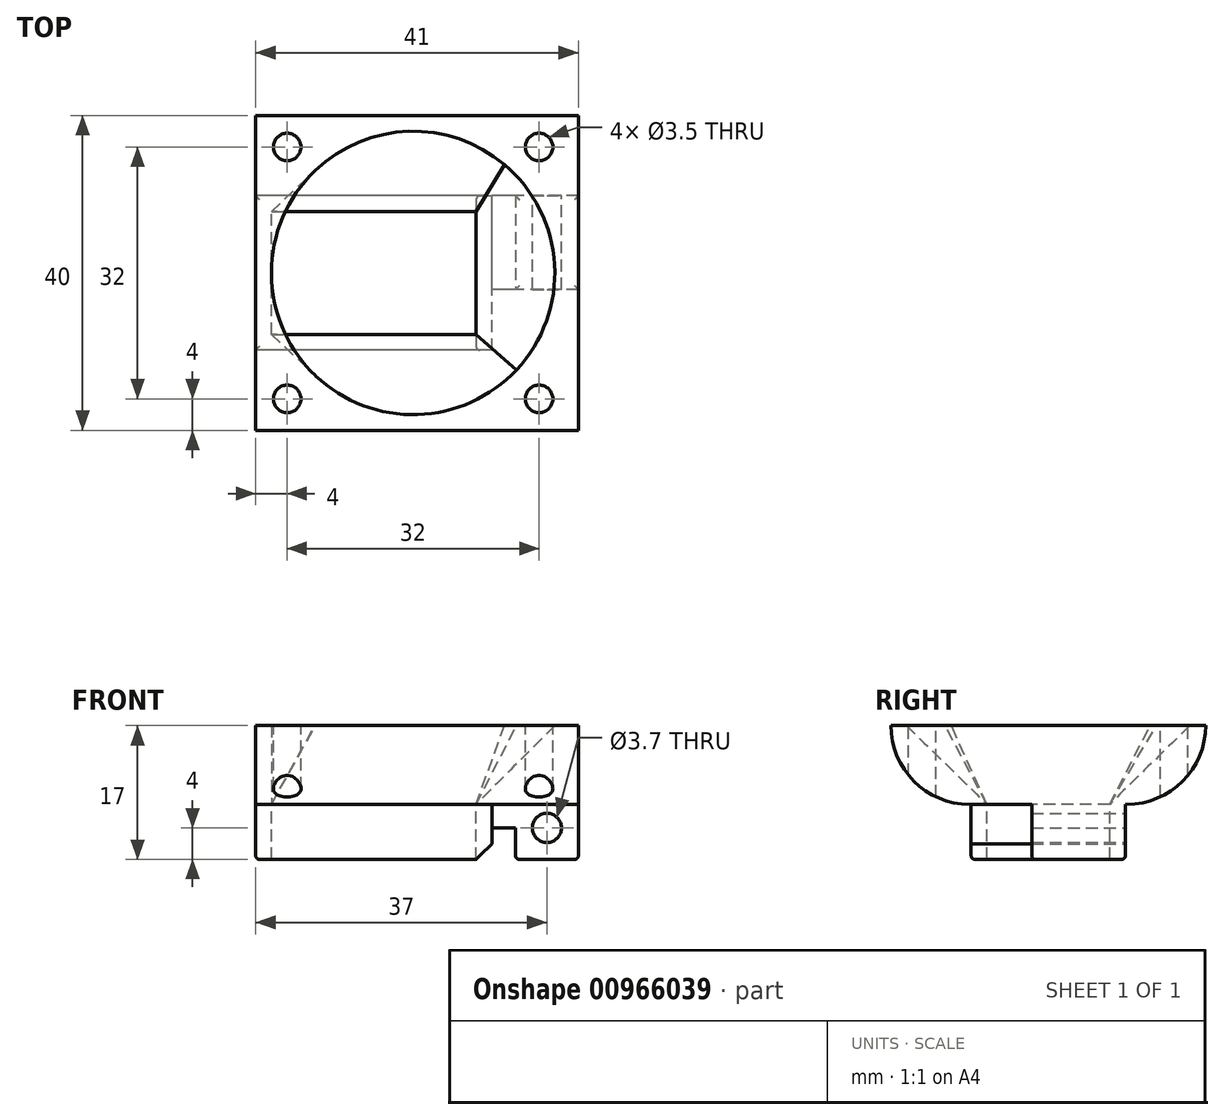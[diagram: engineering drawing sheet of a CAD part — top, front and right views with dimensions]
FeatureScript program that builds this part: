
annotation { "Feature Type Name" : "Feature", "Feature Type Description" : "" }
export const myFeature = defineFeature(function(context is Context, id is Id, definition is map)
    precondition{}
    {
        {
            var Q0;
            Q0=qCreatedBy(makeId("Top.planeOp"),FACE);
            var sketch = newSketch(context, id + "F0", { "sketchPlane" : qUnion([Q0])});
            skLineSegment(sketch, "E0.bottom", {"start": v(20.5, -9.8) * mm, "end": v(-20.5, -9.8) * mm});
            skLineSegment(sketch, "E0.top", {"start": v(20.5, 9.8) * mm, "end": v(-20.5, 9.8) * mm});
            skLineSegment(sketch, "E0.left", {"start": v(20.5, -9.8) * mm, "end": v(20.5, 9.8) * mm});
            skLineSegment(sketch, "E0.right", {"start": v(-20.5, -9.8) * mm, "end": v(-20.5, 9.8) * mm});
            skPoint(sketch, "E0.middle", {"position": v(0, 0) * mm});
            skLineSegment(sketch, "E1.bottom", {"start": v(20.5, -9.8) * mm, "end": v(9.5, -9.8) * mm});
            skLineSegment(sketch, "E1.top", {"start": v(20.5, -2.1) * mm, "end": v(9.5, -2.1) * mm});
            skLineSegment(sketch, "E1.left", {"start": v(20.5, -9.8) * mm, "end": v(20.5, -2.1) * mm});
            skLineSegment(sketch, "E1.right", {"start": v(9.5, -9.8) * mm, "end": v(9.5, -2.1) * mm});
            skSolve(sketch);
        }
        {
            var Q0;
            {var subQ1=sQuery(id+"F0.wireOp",EDGE,"E0.top");Q0=makeQuery(id+"F0.imprint","IMPRINT",FACE,{"disambiguationData":[TD([[makeQuery(id+"F0.imprint","IMPRINT",EDGE,{"derivedFrom":subQ1}),1.0]])]});}
            extrude(context, id + "F1", {"entities" : qUnion([Q0]), "oppositeDirection" : true, "depth" : 3 * mm, "offsetDistance" : 25 * mm});
        }
        {
            var Q0;
            Q0=makeQuery(id+"F1.opExtrude","CAP_FACE",FACE,{"disambiguationData":[OSD([sQuery(id+"F0.wireOp",EDGE,"E0.bottom"),sQuery(id+"F0.wireOp",EDGE,"E0.top"),sQuery(id+"F0.wireOp",EDGE,"E0.left"),sQuery(id+"F0.wireOp",EDGE,"E0.right"),sQuery(id+"F0.wireOp",EDGE,"E1.top"),sQuery(id+"F0.wireOp",EDGE,"E1.right")])],"isStart":false});
            var sketch = newSketch(context, id + "F2", { "sketchPlane" : qUnion([Q0])});
            skLineSegment(sketch, "E2.bottom", {"start": v(-20.5, 9.8) * mm, "end": v(9.5, 9.8) * mm});
            skLineSegment(sketch, "E2.top", {"start": v(-20.5, -9.8) * mm, "end": v(9.5, -9.8) * mm});
            skLineSegment(sketch, "E2.left", {"start": v(-20.5, 9.8) * mm, "end": v(-20.5, -9.8) * mm});
            skLineSegment(sketch, "E2.right", {"start": v(9.5, 9.8) * mm, "end": v(9.5, -9.8) * mm});
            skSolve(sketch);
        }
        {
            var Q0;
            Q0=qSketchRegion(id+"F2",true);
            extrude(context, id + "F3", {"entities" : qUnion([Q0]), "operationType" : NewBodyOperationType.ADD, "depth" : 4 * mm, "offsetDistance" : 25 * mm});
        }
        {
            var Q0;
            Q0=makeQuery(id+"F1.opExtrude","CAP_FACE",FACE,{"disambiguationData":[OSD([sQuery(id+"F0.wireOp",EDGE,"E0.bottom"),sQuery(id+"F0.wireOp",EDGE,"E0.top"),sQuery(id+"F0.wireOp",EDGE,"E0.left"),sQuery(id+"F0.wireOp",EDGE,"E0.right"),sQuery(id+"F0.wireOp",EDGE,"E1.top"),sQuery(id+"F0.wireOp",EDGE,"E1.right")])],"isStart":false});
            var sketch = newSketch(context, id + "F4", { "sketchPlane" : qUnion([Q0])});
            skLineSegment(sketch, "E3.bottom", {"start": v(20.5, -9.8) * mm, "end": v(12.5, -9.8) * mm});
            skLineSegment(sketch, "E3.top", {"start": v(20.5, 2.1) * mm, "end": v(12.5, 2.1) * mm});
            skLineSegment(sketch, "E3.left", {"start": v(20.5, -9.8) * mm, "end": v(20.5, 2.1) * mm});
            skLineSegment(sketch, "E3.right", {"start": v(12.5, -9.8) * mm, "end": v(12.5, 2.1) * mm});
            skSolve(sketch);
        }
        {
            var Q0;
            Q0=qSketchRegion(id+"F4",true);
            extrude(context, id + "F5", {"entities" : qUnion([Q0]), "operationType" : NewBodyOperationType.ADD, "depth" : 4 * mm, "offsetDistance" : 25 * mm});
        }
        {
            var Q0;
            Q0=makeQuery(id+"F5.boolean.opBoolean","MERGE",FACE,{"derivedFrom":[makeQuery(id+"F3.boolean.opBoolean","MERGE",FACE,{"derivedFrom":[makeQuery(id+"F1.opExtrude","SWEPT_FACE",FACE,{"disambiguationData":[OSD([sQuery(id+"F0.wireOp",EDGE,"E0.top")])]}),makeQuery(id+"F3.opExtrude","SWEPT_FACE",FACE,{"disambiguationData":[OSD([sQuery(id+"F2.wireOp",EDGE,"E2.top")])]})]}),makeQuery(id+"F5.opExtrude","SWEPT_FACE",FACE,{"disambiguationData":[OSD([sQuery(id+"F4.wireOp",EDGE,"E3.bottom")])]})]});
            var sketch = newSketch(context, id + "F6", { "sketchPlane" : qUnion([Q0])});
            skCircle(sketch, "E4", {"center": v(-16.5, -3) * mm, "radius": 1.85 * mm});
            skSolve(sketch);
        }
        {
            var Q0;
            Q0=qSketchRegion(id+"F6",true);
            extrude(context, id + "F7", {"entities" : qUnion([Q0]), "operationType" : NewBodyOperationType.REMOVE, "endBound" : BoundingType.THROUGH_ALL, "oppositeDirection" : true, "depth" : 25 * mm, "offsetDistance" : 25 * mm});
        }
        {
            var Q0;
            Q0=makeQuery(id+"F1.opExtrude","CAP_FACE",FACE,{"disambiguationData":[OSD([sQuery(id+"F0.wireOp",EDGE,"E0.bottom"),sQuery(id+"F0.wireOp",EDGE,"E0.top"),sQuery(id+"F0.wireOp",EDGE,"E0.left"),sQuery(id+"F0.wireOp",EDGE,"E0.right"),sQuery(id+"F0.wireOp",EDGE,"E1.top"),sQuery(id+"F0.wireOp",EDGE,"E1.right")])],"isStart":true});
            var sketch = newSketch(context, id + "F8", { "sketchPlane" : qUnion([Q0])});
            skLineSegment(sketch, "E5.bottom", {"start": v(-18.5, 7.8) * mm, "end": v(7.5, 7.8) * mm});
            skLineSegment(sketch, "E5.top", {"start": v(-18.5, -7.8) * mm, "end": v(7.5, -7.8) * mm});
            skLineSegment(sketch, "E5.left", {"start": v(-18.5, 7.8) * mm, "end": v(-18.5, -7.8) * mm});
            skLineSegment(sketch, "E5.right", {"start": v(7.5, 7.8) * mm, "end": v(7.5, -7.8) * mm});
            skSolve(sketch);
        }
        {
            var Q0;
            Q0=qSketchRegion(id+"F8",true);
            extrude(context, id + "F9", {"entities" : qUnion([Q0]), "operationType" : NewBodyOperationType.REMOVE, "endBound" : BoundingType.THROUGH_ALL, "oppositeDirection" : true, "depth" : 25 * mm, "offsetDistance" : 25 * mm});
        }
        {
            var Q0;
            Q0=makeQuery(id+"F1.opExtrude","CAP_FACE",FACE,{"disambiguationData":[OSD([sQuery(id+"F0.wireOp",EDGE,"E0.bottom"),sQuery(id+"F0.wireOp",EDGE,"E0.top"),sQuery(id+"F0.wireOp",EDGE,"E0.left"),sQuery(id+"F0.wireOp",EDGE,"E0.right"),sQuery(id+"F0.wireOp",EDGE,"E1.top"),sQuery(id+"F0.wireOp",EDGE,"E1.right")])],"isStart":true});
            var sketch = newSketch(context, id + "F10", { "sketchPlane" : qUnion([Q0])});
            skLineSegment(sketch, "E6.bottom", {"start": v(20.5, -20) * mm, "end": v(-20.5, -20) * mm});
            skLineSegment(sketch, "E6.top", {"start": v(20.5, 20) * mm, "end": v(-20.5, 20) * mm});
            skLineSegment(sketch, "E6.left", {"start": v(20.5, -20) * mm, "end": v(20.5, 20) * mm});
            skLineSegment(sketch, "E6.right", {"start": v(-20.5, -20) * mm, "end": v(-20.5, 20) * mm});
            skPoint(sketch, "E6.middle", {"position": v(0, 0) * mm});
            skSolve(sketch);
        }
        {
            var Q0;
            Q0=qSketchRegion(id+"F10",true);
            extrude(context, id + "F11", {"entities" : qUnion([Q0]), "operationType" : NewBodyOperationType.ADD, "depth" : 10 * mm, "offsetDistance" : 25 * mm});
        }
        {
            var Q0;
            Q0=makeQuery(id+"F11.opExtrude","CAP_FACE",FACE,{"disambiguationData":[OSD([sQuery(id+"F10.wireOp",EDGE,"E6.bottom"),sQuery(id+"F10.wireOp",EDGE,"E6.top"),sQuery(id+"F10.wireOp",EDGE,"E6.left"),sQuery(id+"F10.wireOp",EDGE,"E6.right")])],"isStart":false});
            var sketch = newSketch(context, id + "F12", { "sketchPlane" : qUnion([Q0])});
            skArc(sketch, "E7", {"start": v(-13, 12.96) * mm, "mid": v(-18.5, -0.07) * mm, "end": v(-12.9, -13.05) * mm});
            skArc(sketch, "E8", {"start": v(11.1, 13.77) * mm, "mid": v(-1.1, 17.99) * mm, "end": v(-13, 12.96) * mm});
            skArc(sketch, "E9", {"start": v(12.63, -12.3) * mm, "mid": v(17.47, 1.06) * mm, "end": v(11.1, 13.77) * mm});
            skArc(sketch, "E10", {"start": v(-12.9, -13.05) * mm, "mid": v(0.02, -18) * mm, "end": v(12.63, -12.3) * mm});
            skSolve(sketch);
        }
        {
            var Q1;
            Q1=qSketchRegion(id+"F8",true);
            var Q2;
            Q2=makeQuery(id+"F12.imprint","IMPRINT",FACE,{"disambiguationData":[TD([[makeQuery(id+"F12.imprint","IMPRINT",EDGE,{"derivedFrom":sQuery(id+"F12.wireOp",EDGE,"E7")}),1.0]])]});
            loft(context, id + "F13", {"operationType" : NewBodyOperationType.REMOVE, "sheetProfilesArray" : [{ "sheetProfileEntities" : qUnion([Q1]) }, { "sheetProfileEntities" : qUnion([Q2]) }]});
        }
        {
            var Q0;
            Q0=makeQuery(id+"F11.opExtrude","CAP_EDGE",EDGE,{"disambiguationData":[OSD([sQuery(id+"F10.wireOp",EDGE,"E6.bottom")])],"isStart":true});
            var Q1;
            Q1=makeQuery(id+"F11.opExtrude","CAP_EDGE",EDGE,{"disambiguationData":[OSD([sQuery(id+"F10.wireOp",EDGE,"E6.top")])],"isStart":true});
            fillet(context, id + "F14", {"entities" : qUnion([Q0, Q1]), "radius" : 10 * mm, "rho" : 0, "crossSection" : FilletCrossSection.CONIC, "allowEdgeOverflow" : false});
        }
        {
            var Q0;
            Q0=makeQuery(id+"F11.opExtrude","CAP_FACE",FACE,{"disambiguationData":[OSD([sQuery(id+"F10.wireOp",EDGE,"E6.bottom"),sQuery(id+"F10.wireOp",EDGE,"E6.top"),sQuery(id+"F10.wireOp",EDGE,"E6.left"),sQuery(id+"F10.wireOp",EDGE,"E6.right")])],"isStart":false});
            var sketch = newSketch(context, id + "F15", { "sketchPlane" : qUnion([Q0])});
            skCircle(sketch, "E11", {"center": v(-16.5, 16) * mm, "radius": 1.75 * mm});
            skCircle(sketch, "E12", {"center": v(15.5, 16) * mm, "radius": 1.75 * mm});
            skCircle(sketch, "E13", {"center": v(15.5, -16) * mm, "radius": 1.75 * mm});
            skCircle(sketch, "E14", {"center": v(-16.5, -16) * mm, "radius": 1.75 * mm});
            skSolve(sketch);
        }
        {
            var Q0;
            Q0=qSketchRegion(id+"F15",true);
            extrude(context, id + "F16", {"entities" : qUnion([Q0]), "operationType" : NewBodyOperationType.REMOVE, "endBound" : BoundingType.THROUGH_ALL, "oppositeDirection" : true, "depth" : 25 * mm, "offsetDistance" : 25 * mm});
        }
        {
            var Q0;
            Q0=makeQuery(id+"F3.opExtrude","CAP_EDGE",EDGE,{"disambiguationData":[OSD([sQuery(id+"F2.wireOp",EDGE,"E2.right")])],"isStart":false});
            chamfer(context, id + "F17", {"entities" : qUnion([Q0]), "width" : 2 * mm, "tangentPropagation" : true});
        }
        {
            var Q0;
            Q0=makeQuery(id+"F3.opExtrude","CAP_EDGE",EDGE,{"disambiguationData":[OSD([sQuery(id+"F2.wireOp",EDGE,"E2.top")])],"isStart":false});
            var Q1;
            Q1=makeQuery(id+"F3.opExtrude","CAP_EDGE",EDGE,{"disambiguationData":[OSD([sQuery(id+"F2.wireOp",EDGE,"E2.left")])],"isStart":false});
            var Q2;
            Q2=makeQuery(id+"F3.opExtrude","CAP_EDGE",EDGE,{"disambiguationData":[OSD([sQuery(id+"F2.wireOp",EDGE,"E2.bottom")])],"isStart":false});
            var Q3;
            Q3=makeQuery(id+"F5.opExtrude","CAP_EDGE",EDGE,{"disambiguationData":[OSD([sQuery(id+"F4.wireOp",EDGE,"E3.top")])],"isStart":false});
            var Q4;
            Q4=makeQuery(id+"F5.opExtrude","CAP_EDGE",EDGE,{"disambiguationData":[OSD([sQuery(id+"F4.wireOp",EDGE,"E3.right")])],"isStart":false});
            var Q5;
            Q5=makeQuery(id+"F5.opExtrude","CAP_EDGE",EDGE,{"disambiguationData":[OSD([sQuery(id+"F4.wireOp",EDGE,"E3.bottom")])],"isStart":false});
            var Q6;
            Q6=makeQuery(id+"F5.opExtrude","CAP_EDGE",EDGE,{"disambiguationData":[OSD([sQuery(id+"F4.wireOp",EDGE,"E3.left")])],"isStart":false});
            fillet(context, id + "F18", {"entities" : qUnion([Q0, Q1, Q2, Q3, Q4, Q5, Q6]), "radius" : .5 * mm, "tangentPropagation" : true, "allowEdgeOverflow" : false});
        }
    });
